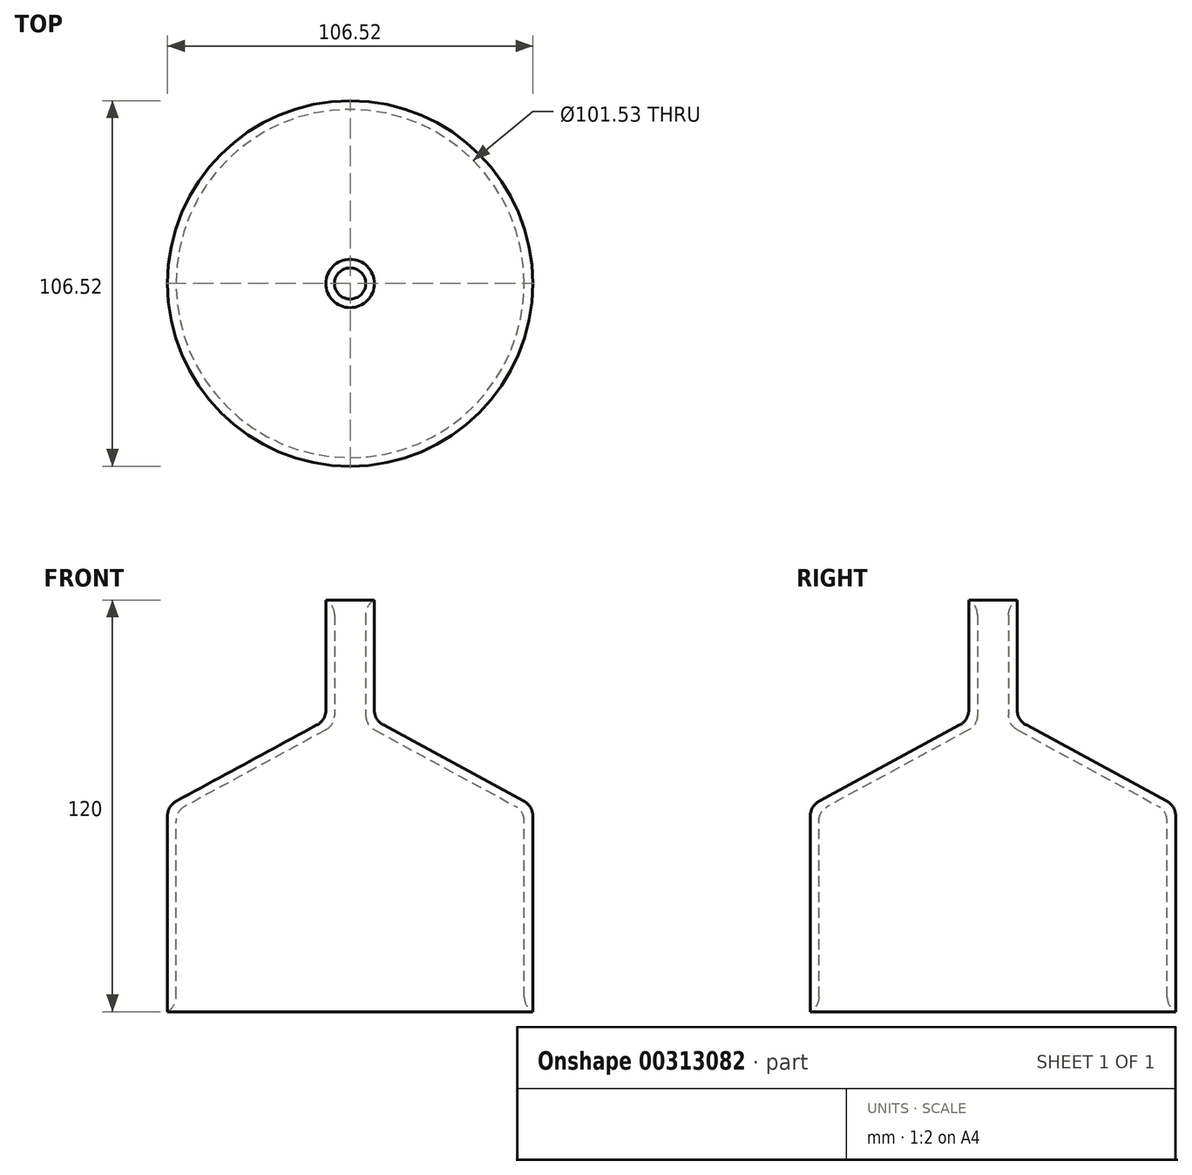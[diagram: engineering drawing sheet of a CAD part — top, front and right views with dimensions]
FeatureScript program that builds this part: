
annotation { "Feature Type Name" : "Feature", "Feature Type Description" : "" }
export const myFeature = defineFeature(function(context is Context, id is Id, definition is map)
    precondition{}
    {
        {
            var Q0;
            Q0=qCreatedBy(makeId("Top.planeOp"),FACE);
            var sketch = newSketch(context, id + "F0", { "sketchPlane" : qUnion([Q0])});
            skCircle(sketch, "E0", {"center": v(0, 0) * mm, "radius": 53.26 * mm});
            skSolve(sketch);
        }
        {
            var Q0;
            Q0=qCreatedBy(makeId("Top.planeOp"),FACE);
            cPlane(context, id + "F1", {"entities" : qUnion([Q0]), "cplaneType" : CPlaneType.OFFSET, "offset" : 25 * mm, "width" : 150 * mm, "height" : 150 * mm});
        }
        {
            var Q0;
            Q0=qCreatedBy(id+"F1.planeOp",FACE);
            var sketch = newSketch(context, id + "F2", { "sketchPlane" : qUnion([Q0])});
            skCircle(sketch, "E1", {"center": v(0, 0) * mm, "radius": 7.05 * mm});
            skSolve(sketch);
        }
        {
            var Q0;
            Q0=makeQuery(id+"F2.imprint","IMPRINT",FACE,{"disambiguationData":[TD([[makeQuery(id+"F2.imprint","IMPRINT",EDGE,{"derivedFrom":sQuery(id+"F2.wireOp",EDGE,"E1")}),1.0]])]});
            var Q1;
            Q1=makeQuery(id+"F0.imprint","IMPRINT",FACE,{"disambiguationData":[TD([[makeQuery(id+"F0.imprint","IMPRINT",EDGE,{"derivedFrom":sQuery(id+"F0.wireOp",EDGE,"E0")}),1.0]])]});
            loft(context, id + "F3", {"sheetProfilesArray" : [{ "sheetProfileEntities" : qUnion([Q0]) }, { "sheetProfileEntities" : qUnion([Q1]) }]});
        }
        {
            var Q0;
            Q0=makeQuery(id+"F3.opLoft","CAP_FACE",FACE,{"disambiguationData":[OSD([makeQuery(id+"F2.imprint","IMPRINT",FACE,{"disambiguationData":[TD([[makeQuery(id+"F2.imprint","IMPRINT",EDGE,{"derivedFrom":sQuery(id+"F2.wireOp",EDGE,"E1")}),1.0]])]})])],"isStart":true});
            extrude(context, id + "F4", {"entities" : qUnion([Q0]), "operationType" : NewBodyOperationType.ADD, "depth" : 35 * mm});
        }
        {
            var Q0;
            Q0 = qSketchRegion(id + "F0", true);
            extrude(context, id + "F5", {"entities" : qUnion([Q0]), "operationType" : NewBodyOperationType.ADD, "oppositeDirection" : true, "depth" : 60 * mm});
        }
        {
            var Q0;
            Q0=makeQuery(id+"F4.opExtrude","CAP_FACE",FACE,{"disambiguationData":[OSD([makeQuery(id+"F2.imprint","IMPRINT",FACE,{"disambiguationData":[TD([[makeQuery(id+"F2.imprint","IMPRINT",EDGE,{"derivedFrom":sQuery(id+"F2.wireOp",EDGE,"E1")}),1.0]])]})])],"isStart":false});
            var Q1;
            Q1=makeQuery(id+"F3.opLoft","CAP_FACE",FACE,{"disambiguationData":[OSD([makeQuery(id+"F0.imprint","IMPRINT",FACE,{"disambiguationData":[TD([[makeQuery(id+"F0.imprint","IMPRINT",EDGE,{"derivedFrom":sQuery(id+"F0.wireOp",EDGE,"E0")}),1.0]])]})])],"isStart":true});
            var Q2;
            Q2=makeQuery(id+"F5.opExtrude","CAP_FACE",FACE,{"disambiguationData":[OSD([sQuery(id+"F0.wireOp",EDGE,"E0")])],"isStart":false});
            shell(context, id + "F6", {"entities" : qUnion([Q0, Q1, Q2]), "thickness" : 2.5 * mm});
        }
        {
            var Q0;
            {var subQ0=sQuery(id+"F0.wireOp",EDGE,"E0");Q0=makeQuery(id+"F5.boolean.opBoolean","MERGE",EDGE,{"derivedFrom":[makeQuery(id+"F3.opLoft","MID_CAP_EDGE",EDGE,{"disambiguationData":[OSD([subQ0,sQuery(id+"F2.wireOp",EDGE,"E1")])],"capPos":1.0}),makeQuery(id+"F5.opExtrude","CAP_EDGE",EDGE,{"disambiguationData":[OSD([subQ0])],"isStart":true})]});}
            var Q1;
            Q1=makeQuery(id+"F6.opShell","OFFSET_EDGE",EDGE,{"disambiguationData":[OSD([sQuery(id+"F0.wireOp",EDGE,"E0")])]});
            var Q2;
            Q2=makeQuery(id+"F6.opShell","OFFSET_FACE",FACE,{"disambiguationData":[OSD([sQuery(id+"F0.wireOp",EDGE,"E0"),sQuery(id+"F2.wireOp",EDGE,"E1")])]});
            var Q3;
            {var subQ0=sQuery(id+"F2.wireOp",EDGE,"E1");Q3=makeQuery(id+"F4.boolean.opBoolean","MERGE",EDGE,{"derivedFrom":[makeQuery(id+"F3.opLoft","MID_CAP_EDGE",EDGE,{"disambiguationData":[OSD([subQ0])],"capPos":0.0}),makeQuery(id+"F4.opExtrude","CAP_EDGE",EDGE,{"disambiguationData":[OSD([subQ0])],"isStart":true})]});}
            var Q4;
            Q4=makeQuery(id+"F6.opShell","OFFSET_FACE",FACE,{"disambiguationData":[OSD([sQuery(id+"F2.wireOp",EDGE,"E1")])]});
            fillet(context, id + "F7", {"entities" : qUnion([Q0, Q1, Q2, Q3, Q4]), "radius" : 5 * mm, "allowEdgeOverflow" : false});
        }
    });
